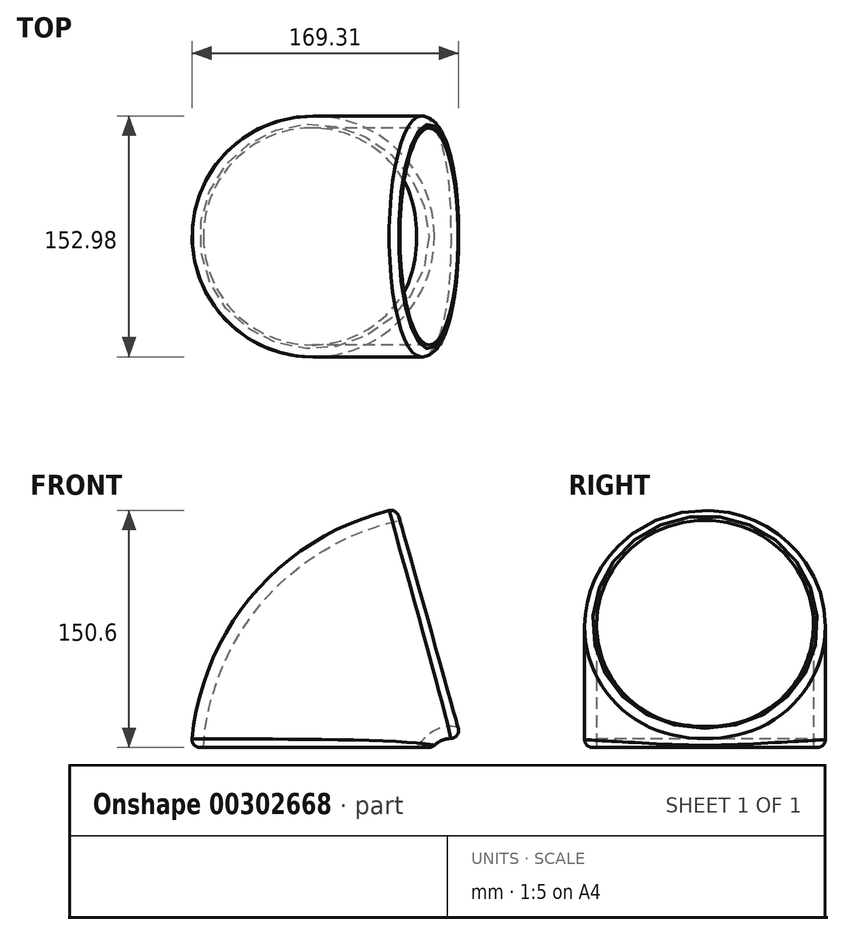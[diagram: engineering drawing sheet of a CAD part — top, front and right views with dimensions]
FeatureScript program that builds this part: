
annotation { "Feature Type Name" : "Feature", "Feature Type Description" : "" }
export const myFeature = defineFeature(function(context is Context, id is Id, definition is map)
    precondition{}
    {
        {
            var Q0;
            Q0=qCreatedBy(makeId("Top.planeOp"),FACE);
            var sketch = newSketch(context, id + "F0", { "sketchPlane" : qUnion([Q0])});
            skCircle(sketch, "E0", {"center": v(0, 0) * mm, "radius": 76.49 * mm});
            skSolve(sketch);
        }
        {
            var Q0;
            Q0=qCreatedBy(makeId("Front.planeOp"),FACE);
            var sketch = newSketch(context, id + "F1", { "sketchPlane" : qUnion([Q0])});
            skArc(sketch, "E1", {"start": v(74.58, 77.93) * mm, "mid": v(24.2, 51.5) * mm, "end": v(0, 0) * mm});
            skSolve(sketch);
        }
        {
            var Q0;
            Q0=makeQuery(id+"F0.imprint","IMPRINT",FACE,{"disambiguationData":[TD([[makeQuery(id+"F0.imprint","IMPRINT",EDGE,{"derivedFrom":sQuery(id+"F0.wireOp",EDGE,"E0")}),1.0]])]});
            var Q1;
            Q1=sQuery(id+"F1.wireOp",EDGE,"E1");
            sweep(context, id + "F2", {"profiles" : qUnion([Q0]), "path" : qUnion([Q1])});
        }
        {
            var Q0;
            Q0=makeQuery(id+"F2.opSweep","CAP_FACE",FACE,{"disambiguationData":[OSD([sQuery(id+"F0.wireOp",EDGE,"E0"),sQuery(id+"F1.wireOp",VERTEX,"E1.start")])],"isStart":false});
            var Q1;
            Q1=makeQuery(id+"F2.opSweep","CAP_FACE",FACE,{"disambiguationData":[OSD([sQuery(id+"F0.wireOp",EDGE,"E0"),sQuery(id+"F1.wireOp",VERTEX,"E1.end")])],"isStart":true});
            shell(context, id + "F3", {"entities" : qUnion([Q0, Q1]), "thickness" : 7.62 * mm});
        }
        {
            var Q0;
            Q0=makeQuery(id+"F2.opSweep","CAP_EDGE",EDGE,{"disambiguationData":[OSD([sQuery(id+"F0.wireOp",EDGE,"E0"),sQuery(id+"F1.wireOp",VERTEX,"E1.start")])],"isStart":false});
            var Q1;
            Q1=makeQuery(id+"F2.opSweep","CAP_EDGE",EDGE,{"disambiguationData":[OSD([sQuery(id+"F0.wireOp",EDGE,"E0"),sQuery(id+"F1.wireOp",VERTEX,"E1.end")])],"isStart":true});
            fillet(context, id + "F4", {"entities" : qUnion([Q0, Q1]), "radius" : 5.08 * mm, "tangentPropagation" : true, "allowEdgeOverflow" : false});
        }
    });
